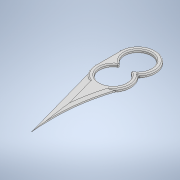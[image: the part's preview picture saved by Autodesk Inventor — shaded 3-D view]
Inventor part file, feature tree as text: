
AUTODESK INVENTOR PART (.ipt)
format: ipt  version: 2020 (Build 240168000, 168)  size: 212,480 bytes
history: native  units: in
note: dims shown in document units (in); Inventor stores cm internally (conversion verified against a paired STEP export)
features: chamfer x4, fillet x2, extrude x1, sketch x1
ambient origin geometry x8: Origin, YZ Plane, XZ Plane, XY Plane, X Axis, Y Axis, Z Axis, Center Point
bodies: Solid1 (feature_tree)
feature tree (8):
  extrude  "Extrusion1"  Depth=0.7in
  chamfer  "Chamfer1"  Distance=0.75in
  chamfer  "Chamfer2"  Distance=1.0in
  chamfer  "Chamfer3"  Distance=1.0in
  chamfer  "Chamfer4"  Distance=2.0in
  fillet  "Fillet5"  Radius=0.2in
  fillet  "Fillet6"  Radius=0.1in
  sketch  "Sketch1"  dims[d0=0.75in d1=0.7in d2=0.75in d3=1.0in d4=1.0in d5=2.0in d6=0.2in d7=0.1in d8=0.0in d9=0.2in d10=0.05in d11=45.0deg d12=0.2in d13=0.05in d14=45.0deg d15=0.1in d16=0.03in d17=45.0deg d18=0.1in d19=0.03in d20=45.0deg d25=0.03in d26=0.03in]
